# Revit family: Kabelrinne SKS
name_source: partatom
category: Generic Models
revit_build: Autodesk Revit 2015 (Build: 20140606_1530(x64)
units: mm (PartAtom-declared; Revit-internal decimal feet)

## types (12) — shared parameters
Height = 105 mm  [stored 0.344488 ft]
Length = 3000 mm  [stored 9.84252 ft]
Manufacturer = OBO Bettermann
URL = http://www.obo-bettermann.com

## per-type parameters (varying)
| type | GTIN | Manufacturer Art.No. | Material | Width |
| SKS 110 FS | 4012196062171 | 6061109 | Strip-galvanised | 100 mm  [stored 0.328084 ft] |
| SKS 120 FS | 4012196062232 | 6061206 | Strip-galvanised | 200 mm  [stored 0.656168 ft] |
| SKS 130 FS | 4012196062294 | 6061303 | Strip-galvanised | 300 mm |
| SKS 140 FS | 4012196062355 | 6061400 | Strip-galvanised | 400 mm  [stored 1.31234 ft] |
| SKS 150 FS | 4012196062416 | 6061508 | Strip-galvanised | 500 mm  [stored 1.64042 ft] |
| SKS 155 FS | 4012196062478 | 6061559 | Strip-galvanised | 550 mm |
| SKS 110 FT | 4012196062539 | 6061605 | Hot-dip galvanised | 100 mm  [stored 0.328084 ft] |
| SKS 120 FT | 4012196062591 | 6061621 | Hot-dip galvanised | 200 mm  [stored 0.656168 ft] |
| SKS 130 FT | 4012196062652 | 6061656 | Hot-dip galvanised | 300 mm |
| SKS 140 FT | 4012196062713 | 6061672 | Hot-dip galvanised | 400 mm  [stored 1.31234 ft] |
| SKS 150 FT | 4012196062775 | 6061702 | Hot-dip galvanised | 500 mm  [stored 1.64042 ft] |
| SKS 155 FT | 4012196062836 | 6061729 | Hot-dip galvanised | 550 mm |

note: column(s) folded — value = type name in every type: Article Type

note: [stored X ft] marks values corroborated as IEEE doubles in the binary element streams (Revit-internal decimal feet)

## geometry (parser evidence)
native form markers: Sweep x3
no freeform markers — native parametric forms only
